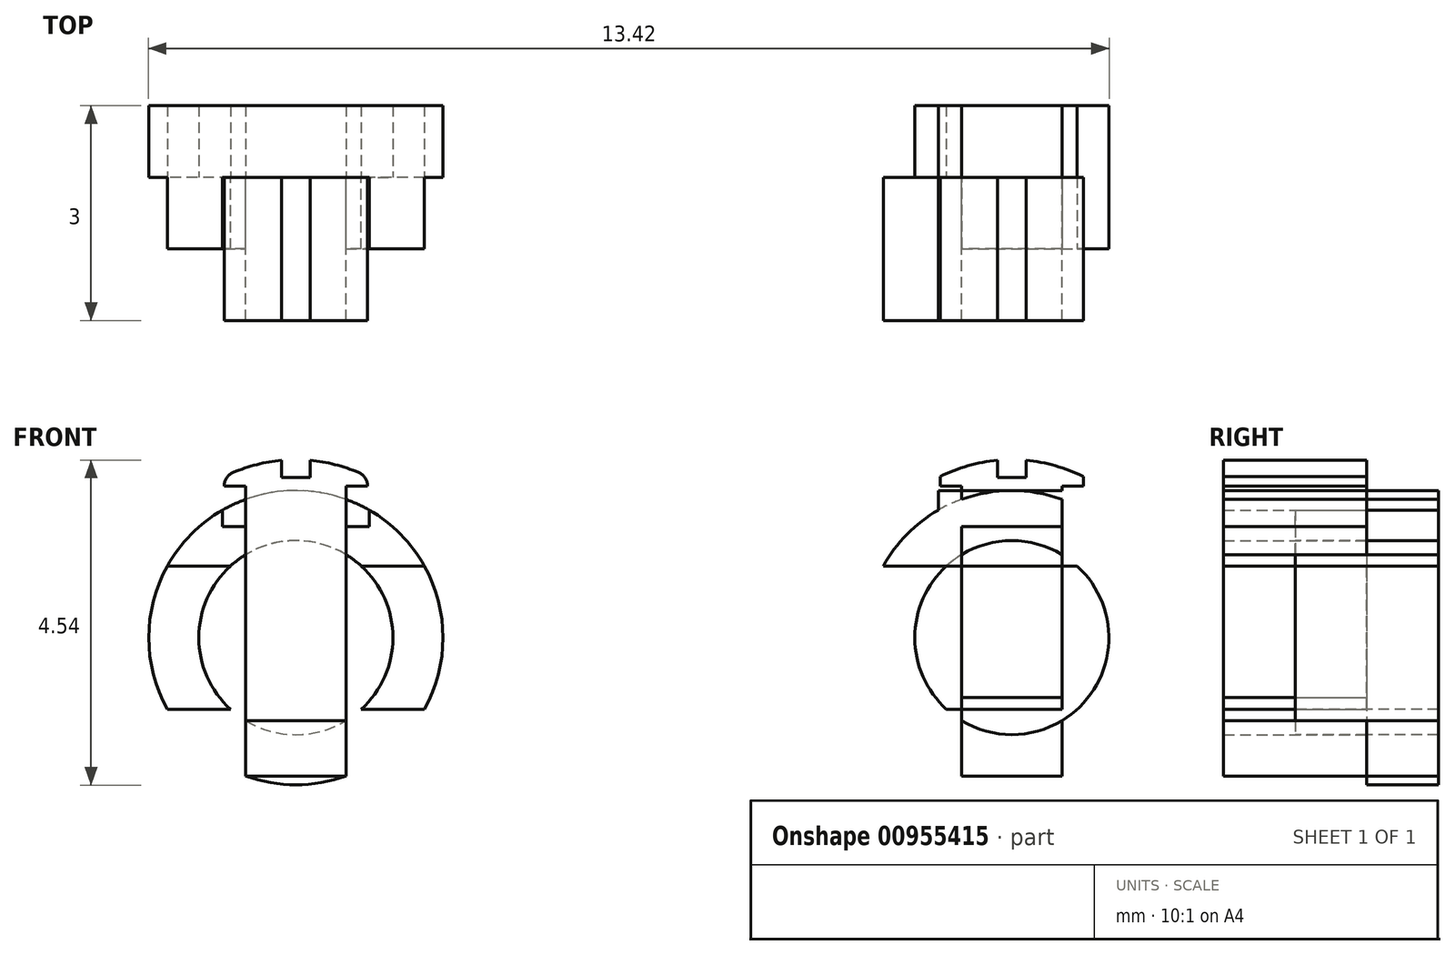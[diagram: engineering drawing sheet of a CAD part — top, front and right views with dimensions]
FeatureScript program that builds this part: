
annotation { "Feature Type Name" : "Feature", "Feature Type Description" : "" }
export const myFeature = defineFeature(function(context is Context, id is Id, definition is map)
    precondition{}
    {
        {
            var Q0;
            Q0=qCreatedBy(makeId("Front.planeOp"),FACE);
            var sketch = newSketch(context, id + "F0", { "sketchPlane" : qUnion([Q0])});
            skCircle(sketch, "E0", {"center": v(0, 0) * mm, "radius": 2.06 * mm});
            skLineSegment(sketch, "E1.bottom", {"start": v(2.5, 1) * mm, "end": v(-2.5, 1) * mm});
            skLineSegment(sketch, "E1.top", {"start": v(2.5, -1) * mm, "end": v(-2.5, -1) * mm});
            skLineSegment(sketch, "E1.left", {"start": v(2.5, 1) * mm, "end": v(2.5, -1) * mm});
            skLineSegment(sketch, "E1.right", {"start": v(-2.5, 1) * mm, "end": v(-2.5, -1) * mm});
            skCircle(sketch, "E2", {"center": v(0, 0) * mm, "radius": 1.35 * mm});
            skPoint(sketch, "E3", {"position": v(0, -1.35) * mm});
            skPoint(sketch, "E4", {"position": v(0, -2.06) * mm});
            skLineSegment(sketch, "E5.bottom", {"start": v(-0.7, 2.48) * mm, "end": v(0.7, 2.48) * mm});
            skLineSegment(sketch, "E5.top", {"start": v(-0.7, -1.93) * mm, "end": v(0.7, -1.93) * mm});
            skLineSegment(sketch, "E5.left", {"start": v(-0.7, 2.48) * mm, "end": v(-0.7, -1.93) * mm});
            skLineSegment(sketch, "E5.right", {"start": v(0.7, 2.48) * mm, "end": v(0.7, -1.93) * mm});
            skLineSegment(sketch, "E6.bottom", {"start": v(-1, 2.48) * mm, "end": v(1, 2.48) * mm});
            skLineSegment(sketch, "E6.top", {"start": v(-1, 2.11) * mm, "end": v(1, 2.11) * mm});
            skLineSegment(sketch, "E6.left", {"start": v(-1, 2.48) * mm, "end": v(-1, 2.11) * mm});
            skLineSegment(sketch, "E6.right", {"start": v(1, 2.48) * mm, "end": v(1, 2.11) * mm});
            skLineSegment(sketch, "E7", {"start": v(-0.7, -1.35) * mm, "end": v(0.7, -1.35) * mm});
            skPoint(sketch, "E8", {"position": v(-0.7, -1.16) * mm});
            skPoint(sketch, "E9", {"position": v(0.7, -1.16) * mm});
            skLineSegment(sketch, "E10", {"start": v(-0.7, -1.16) * mm, "end": v(0.7, -1.16) * mm});
            skLineSegment(sketch, "E11", {"start": v(5, 2.95) * mm, "end": v(5, -2.35) * mm});
            skLineSegment(sketch, "E12.MirrorCS", {"start": v(7.5, 1) * mm, "end": v(7.5, -1) * mm});
            skCircle(sketch, "E13.MirrorC", {"center": v(10, 0) * mm, "radius": 1.35 * mm});
            skLineSegment(sketch, "E14.MirrorCS", {"start": v(7.5, 1) * mm, "end": v(12.5, 1) * mm});
            skLineSegment(sketch, "E15.MirrorCS", {"start": v(7.5, -1) * mm, "end": v(12.5, -1) * mm});
            skLineSegment(sketch, "E16.MirrorCS", {"start": v(12.5, 1) * mm, "end": v(12.5, -1) * mm});
            skCircle(sketch, "E17.MirrorC", {"center": v(10, 0) * mm, "radius": 2.06 * mm});
            skLineSegment(sketch, "E18.MirrorCS", {"start": v(11, 2.49) * mm, "end": v(9, 2.49) * mm});
            skLineSegment(sketch, "E19.MirrorCS", {"start": v(11, 2.12) * mm, "end": v(9, 2.12) * mm});
            skLineSegment(sketch, "E20.MirrorCS", {"start": v(10.7, 2.49) * mm, "end": v(10.7, -1.93) * mm});
            skLineSegment(sketch, "E21.MirrorCS", {"start": v(9.3, 2.49) * mm, "end": v(9.3, -1.93) * mm});
            skLineSegment(sketch, "E22.MirrorCS", {"start": v(9, 2.49) * mm, "end": v(9, 2.12) * mm});
            skLineSegment(sketch, "E23.MirrorCS", {"start": v(11, 2.49) * mm, "end": v(11, 2.12) * mm});
            skLineSegment(sketch, "E24.MirrorCS", {"start": v(10.7, -1.93) * mm, "end": v(9.3, -1.93) * mm});
            skPoint(sketch, "E25", {"position": v(10, -2.06) * mm});
            skPoint(sketch, "E25.positionSnap0", {"position": v(10, -1.93) * mm});
            skLineSegment(sketch, "E26", {"start": v(9.3, -0.84) * mm, "end": v(10.7, -0.84) * mm});
            skLineSegment(sketch, "E27", {"start": v(9.3, -1.94) * mm, "end": v(10.7, -1.94) * mm});
            skPoint(sketch, "E28", {"position": v(9.3, -1.16) * mm});
            skLineSegment(sketch, "E29", {"start": v(10.7, -1.93) * mm, "end": v(10.7, -1.94) * mm});
            skLineSegment(sketch, "E30", {"start": v(9.3, -1.93) * mm, "end": v(9.3, -1.94) * mm});
            skLineSegment(sketch, "E31.bottom", {"start": v(-1.03, 1.55) * mm, "end": v(1.02, 1.55) * mm});
            skLineSegment(sketch, "E31.top", {"start": v(-1.03, 2.06) * mm, "end": v(1.02, 2.06) * mm});
            skLineSegment(sketch, "E31.left", {"start": v(-1.03, 1.55) * mm, "end": v(-1.03, 2.06) * mm});
            skLineSegment(sketch, "E31.right", {"start": v(1.02, 1.55) * mm, "end": v(1.02, 2.06) * mm});
            skLineSegment(sketch, "E32.MirrorCS", {"start": v(11.03, 1.55) * mm, "end": v(8.97, 1.55) * mm});
            skLineSegment(sketch, "E33.MirrorCS", {"start": v(8.97, 1.55) * mm, "end": v(8.97, 2.06) * mm});
            skLineSegment(sketch, "E34.MirrorCS", {"start": v(11.03, 2.06) * mm, "end": v(8.97, 2.06) * mm});
            skLineSegment(sketch, "E35.MirrorCS", {"start": v(11.03, 1.55) * mm, "end": v(11.03, 2.06) * mm});
            skSolve(sketch);
        }
        {
            var Q0;
            {var subQ0=sQuery(id+"F0.wireOp",EDGE,"E5.left");var subQ1=sQuery(id+"F0.wireOp",EDGE,"E0");var subQ2=makeQuery(id+"F0.imprint","INTERSECT",VERTEX,{"derivedFrom":[subQ1,subQ0]});Q0=makeQuery(id+"F0.imprint","IMPRINT",FACE,{"disambiguationData":[TD([[makeQuery(id+"F0.imprint","IMPRINT",EDGE,{"disambiguationData":[TD([[subQ2,-1.0]])],"derivedFrom":subQ1}),1.0]])]});}
            var Q1;
            {var subQ0=sQuery(id+"F0.wireOp",EDGE,"E5.right");var subQ1=sQuery(id+"F0.wireOp",EDGE,"E0");var subQ2=makeQuery(id+"F0.imprint","INTERSECT",VERTEX,{"derivedFrom":[subQ1,subQ0]});Q1=makeQuery(id+"F0.imprint","IMPRINT",FACE,{"disambiguationData":[TD([[makeQuery(id+"F0.imprint","IMPRINT",EDGE,{"disambiguationData":[TD([[subQ2,1.0]])],"derivedFrom":subQ1}),1.0]])]});}
            var Q2;
            {var subQ0=sQuery(id+"F0.wireOp",EDGE,"E1.bottom");var subQ1=sQuery(id+"F0.wireOp",EDGE,"E0");var subQ2=makeQuery(id+"F0.imprint","INTERSECT",VERTEX,{"disambiguationData":[OD(0.0)],"derivedFrom":[subQ1,subQ0]});Q2=makeQuery(id+"F0.imprint","IMPRINT",FACE,{"disambiguationData":[TD([[makeQuery(id+"F0.imprint","IMPRINT",EDGE,{"disambiguationData":[TD([[subQ2,1.0]])],"derivedFrom":subQ1}),1.0]])]});}
            var Q3;
            {var subQ0=sQuery(id+"F0.wireOp",EDGE,"E1.bottom");var subQ1=sQuery(id+"F0.wireOp",EDGE,"E0");var subQ2=makeQuery(id+"F0.imprint","INTERSECT",VERTEX,{"disambiguationData":[OD(1.0)],"derivedFrom":[subQ1,subQ0]});Q3=makeQuery(id+"F0.imprint","IMPRINT",FACE,{"disambiguationData":[TD([[makeQuery(id+"F0.imprint","IMPRINT",EDGE,{"disambiguationData":[TD([[subQ2,-1.0]])],"derivedFrom":subQ1}),1.0]])]});}
            var Q4;
            {var subQ3=sQuery(id+"F0.wireOp",EDGE,"E1.top");var subQ6=sQuery(id+"F0.wireOp",EDGE,"E0");var subQ7=makeQuery(id+"F0.imprint","INTERSECT",VERTEX,{"disambiguationData":[OD(0.0)],"derivedFrom":[subQ6,subQ3]});Q4=makeQuery(id+"F0.imprint","IMPRINT",FACE,{"disambiguationData":[TD([[makeQuery(id+"F0.imprint","IMPRINT",EDGE,{"disambiguationData":[TD([[subQ7,1.0]])],"derivedFrom":subQ3}),1.0]])]});}
            var Q5;
            {var subQ4=sQuery(id+"F0.wireOp",EDGE,"E1.top");var subQ6=sQuery(id+"F0.wireOp",EDGE,"E0");var subQ7=makeQuery(id+"F0.imprint","INTERSECT",VERTEX,{"disambiguationData":[OD(1.0)],"derivedFrom":[subQ6,subQ4]});Q5=makeQuery(id+"F0.imprint","IMPRINT",FACE,{"disambiguationData":[TD([[makeQuery(id+"F0.imprint","IMPRINT",EDGE,{"disambiguationData":[TD([[subQ7,-1.0]])],"derivedFrom":subQ4}),1.0]])]});}
            var Q6;
            {var subQ0=sQuery(id+"F0.wireOp",EDGE,"E5.top");Q6=makeQuery(id+"F0.imprint","IMPRINT",FACE,{"disambiguationData":[TD([[makeQuery(id+"F0.imprint","IMPRINT",EDGE,{"derivedFrom":subQ0}),-1.0]])]});}
            var Q7;
            {var subQ0=sQuery(id+"F0.wireOp",EDGE,"E5.right");var subQ3=sQuery(id+"F0.wireOp",EDGE,"E7");var subQ5=makeQuery(id+"F0.imprint","INTERSECT",VERTEX,{"derivedFrom":[subQ0,subQ3]});Q7=makeQuery(id+"F0.imprint","IMPRINT",FACE,{"disambiguationData":[TD([[makeQuery(id+"F0.imprint","IMPRINT",EDGE,{"disambiguationData":[TD([[subQ5,1.0]])],"derivedFrom":subQ3}),1.0]])]});}
            var Q8;
            {var subQ0=sQuery(id+"F0.wireOp",EDGE,"E5.left");var subQ3=sQuery(id+"F0.wireOp",EDGE,"E7");var subQ5=makeQuery(id+"F0.imprint","INTERSECT",VERTEX,{"derivedFrom":[subQ0,subQ3]});Q8=makeQuery(id+"F0.imprint","IMPRINT",FACE,{"disambiguationData":[TD([[makeQuery(id+"F0.imprint","IMPRINT",EDGE,{"disambiguationData":[TD([[subQ5,-1.0]])],"derivedFrom":subQ3}),1.0]])]});}
            var Q9;
            {var subQ1=sQuery(id+"F0.wireOp",EDGE,"E5.top");Q9=makeQuery(id+"F0.imprint","IMPRINT",FACE,{"disambiguationData":[TD([[makeQuery(id+"F0.imprint","IMPRINT",EDGE,{"derivedFrom":subQ1}),1.0]])]});}
            var Q10;
            {var subQ0=sQuery(id+"F0.wireOp",EDGE,"E5.right");var subQ1=sQuery(id+"F0.wireOp",EDGE,"E0");var subQ2=makeQuery(id+"F0.imprint","INTERSECT",VERTEX,{"derivedFrom":[subQ1,subQ0]});Q10=makeQuery(id+"F0.imprint","IMPRINT",FACE,{"disambiguationData":[TD([[makeQuery(id+"F0.imprint","IMPRINT",EDGE,{"disambiguationData":[TD([[subQ2,-1.0]])],"derivedFrom":subQ1}),1.0]])]});}
            var Q11;
            {var subQ0=sQuery(id+"F0.wireOp",EDGE,"E21.MirrorCS");var subQ1=sQuery(id+"F0.wireOp",EDGE,"E13.MirrorC");var subQ2=makeQuery(id+"F0.imprint","INTERSECT",VERTEX,{"disambiguationData":[OD(0.0)],"derivedFrom":[subQ1,subQ0]});Q11=makeQuery(id+"F0.imprint","IMPRINT",FACE,{"disambiguationData":[TD([[makeQuery(id+"F0.imprint","IMPRINT",EDGE,{"disambiguationData":[TD([[subQ2,1.0]])],"derivedFrom":subQ1}),1.0]])]});}
            var Q12;
            {var subQ0=sQuery(id+"F0.wireOp",EDGE,"3dWky65o-V6J0-wYT3-5itX-CX1B09bc3K4K");var subQ1=sQuery(id+"F0.wireOp",EDGE,"E17.MirrorC");var subQ2=makeQuery(id+"F0.imprint","INTERSECT",VERTEX,{"disambiguationData":[OD(0.0)],"derivedFrom":[subQ1,subQ0]});Q12=makeQuery(id+"F0.imprint","IMPRINT",FACE,{"disambiguationData":[TD([[makeQuery(id+"F0.imprint","IMPRINT",EDGE,{"disambiguationData":[TD([[subQ2,-1.0]])],"derivedFrom":subQ1}),-1.0]])]});}
            var Q13;
            {var subQ0=sQuery(id+"F0.wireOp",EDGE,"E21.MirrorCS");var subQ1=sQuery(id+"F0.wireOp",EDGE,"E13.MirrorC");var subQ2=makeQuery(id+"F0.imprint","INTERSECT",VERTEX,{"disambiguationData":[OD(0.0)],"derivedFrom":[subQ1,subQ0]});Q13=makeQuery(id+"F0.imprint","IMPRINT",FACE,{"disambiguationData":[TD([[makeQuery(id+"F0.imprint","IMPRINT",EDGE,{"disambiguationData":[TD([[subQ2,-1.0]])],"derivedFrom":subQ1}),1.0]])]});}
            var Q14;
            {var subQ0=sQuery(id+"F0.wireOp",EDGE,"E21.MirrorCS");var subQ1=sQuery(id+"F0.wireOp",EDGE,"E17.MirrorC");var subQ2=makeQuery(id+"F0.imprint","INTERSECT",VERTEX,{"derivedFrom":[subQ1,subQ0]});Q14=makeQuery(id+"F0.imprint","IMPRINT",FACE,{"disambiguationData":[TD([[makeQuery(id+"F0.imprint","IMPRINT",EDGE,{"disambiguationData":[TD([[subQ2,-1.0]])],"derivedFrom":subQ1}),-1.0]])]});}
            var Q15;
            {var subQ0=sQuery(id+"F0.wireOp",EDGE,"3dWky65o-V6J0-wYT3-5itX-CX1B09bc3K4K");var subQ1=sQuery(id+"F0.wireOp",EDGE,"E17.MirrorC");var subQ2=makeQuery(id+"F0.imprint","INTERSECT",VERTEX,{"disambiguationData":[OD(1.0)],"derivedFrom":[subQ1,subQ0]});Q15=makeQuery(id+"F0.imprint","IMPRINT",FACE,{"disambiguationData":[TD([[makeQuery(id+"F0.imprint","IMPRINT",EDGE,{"disambiguationData":[TD([[subQ2,1.0]])],"derivedFrom":subQ1}),-1.0]])]});}
            var Q16;
            {var subQ0=sQuery(id+"F0.wireOp",EDGE,"E20.MirrorCS");var subQ1=sQuery(id+"F0.wireOp",EDGE,"E13.MirrorC");var subQ2=makeQuery(id+"F0.imprint","INTERSECT",VERTEX,{"disambiguationData":[OD(0.0)],"derivedFrom":[subQ1,subQ0]});Q16=makeQuery(id+"F0.imprint","IMPRINT",FACE,{"disambiguationData":[TD([[makeQuery(id+"F0.imprint","IMPRINT",EDGE,{"disambiguationData":[TD([[subQ2,-1.0]])],"derivedFrom":subQ1}),1.0]])]});}
            var Q17;
            {var subQ0=sQuery(id+"F0.wireOp",EDGE,"E21.MirrorCS");var subQ1=sQuery(id+"F0.wireOp",EDGE,"E13.MirrorC");var subQ2=makeQuery(id+"F0.imprint","INTERSECT",VERTEX,{"disambiguationData":[OD(1.0)],"derivedFrom":[subQ1,subQ0]});Q17=makeQuery(id+"F0.imprint","IMPRINT",FACE,{"disambiguationData":[TD([[makeQuery(id+"F0.imprint","IMPRINT",EDGE,{"disambiguationData":[TD([[subQ2,-1.0]])],"derivedFrom":subQ1}),1.0]])]});}
            var Q18;
            {var subQ5=sQuery(id+"F0.wireOp",EDGE,"E24.MirrorCS");Q18=makeQuery(id+"F0.imprint","IMPRINT",FACE,{"disambiguationData":[TD([[makeQuery(id+"F0.imprint","IMPRINT",EDGE,{"derivedFrom":subQ5}),-1.0]])]});}
            var Q19;
            {var subQ0=sQuery(id+"F0.wireOp",EDGE,"E15.MirrorCS");var subQ1=sQuery(id+"F0.wireOp",EDGE,"E13.MirrorC");var subQ2=makeQuery(id+"F0.imprint","INTERSECT",VERTEX,{"disambiguationData":[OD(0.0)],"derivedFrom":[subQ1,subQ0]});Q19=makeQuery(id+"F0.imprint","IMPRINT",FACE,{"disambiguationData":[TD([[makeQuery(id+"F0.imprint","IMPRINT",EDGE,{"disambiguationData":[TD([[subQ2,-1.0]])],"derivedFrom":subQ1}),1.0]])]});}
            var Q20;
            {var subQ0=sQuery(id+"F0.wireOp",EDGE,"E14.MirrorCS");var subQ1=sQuery(id+"F0.wireOp",EDGE,"E13.MirrorC");var subQ2=makeQuery(id+"F0.imprint","INTERSECT",VERTEX,{"disambiguationData":[OD(0.0)],"derivedFrom":[subQ1,subQ0]});Q20=makeQuery(id+"F0.imprint","IMPRINT",FACE,{"disambiguationData":[TD([[makeQuery(id+"F0.imprint","IMPRINT",EDGE,{"disambiguationData":[TD([[subQ2,1.0]])],"derivedFrom":subQ1}),1.0]])]});}
            var Q21;
            {var subQ0=sQuery(id+"F0.wireOp",EDGE,"E27");var subQ1=sQuery(id+"F0.wireOp",EDGE,"E17.MirrorC");var subQ2=makeQuery(id+"F0.imprint","INTERSECT",VERTEX,{"disambiguationData":[OD(0.0)],"derivedFrom":[subQ1,subQ0]});Q21=makeQuery(id+"F0.imprint","IMPRINT",FACE,{"disambiguationData":[TD([[makeQuery(id+"F0.imprint","IMPRINT",EDGE,{"disambiguationData":[TD([[subQ2,-1.0]])],"derivedFrom":subQ1}),-1.0]])]});}
            var Q22;
            {var subQ0=sQuery(id+"F0.wireOp",EDGE,"E14.MirrorCS");var subQ1=sQuery(id+"F0.wireOp",EDGE,"E13.MirrorC");var subQ2=makeQuery(id+"F0.imprint","INTERSECT",VERTEX,{"disambiguationData":[OD(1.0)],"derivedFrom":[subQ1,subQ0]});Q22=makeQuery(id+"F0.imprint","IMPRINT",FACE,{"disambiguationData":[TD([[makeQuery(id+"F0.imprint","IMPRINT",EDGE,{"disambiguationData":[TD([[subQ2,-1.0]])],"derivedFrom":subQ1}),1.0]])]});}
            var Q23;
            {var subQ0=sQuery(id+"F0.wireOp",EDGE,"E24.MirrorCS");Q23=makeQuery(id+"F0.imprint","IMPRINT",FACE,{"disambiguationData":[TD([[makeQuery(id+"F0.imprint","IMPRINT",EDGE,{"derivedFrom":subQ0}),1.0]])]});}
            var Q24;
            {var subQ7=sQuery(id+"F0.wireOp",EDGE,"E0");var subQ9=sQuery(id+"F0.wireOp",EDGE,"E31.right");var subQ10=makeQuery(id+"F0.imprint","INTERSECT",VERTEX,{"derivedFrom":[subQ7,subQ9]});Q24=makeQuery(id+"F0.imprint","IMPRINT",FACE,{"disambiguationData":[TD([[makeQuery(id+"F0.imprint","IMPRINT",EDGE,{"disambiguationData":[TD([[subQ10,1.0]])],"derivedFrom":subQ7}),1.0]])]});}
            var Q25;
            {var subQ7=sQuery(id+"F0.wireOp",EDGE,"E31.left");var subQ9=sQuery(id+"F0.wireOp",EDGE,"E0");var subQ11=makeQuery(id+"F0.imprint","INTERSECT",VERTEX,{"derivedFrom":[subQ9,subQ7]});Q25=makeQuery(id+"F0.imprint","IMPRINT",FACE,{"disambiguationData":[TD([[makeQuery(id+"F0.imprint","IMPRINT",EDGE,{"disambiguationData":[TD([[subQ11,-1.0]])],"derivedFrom":subQ9}),1.0]])]});}
            var Q26;
            {var subQ0=sQuery(id+"F0.wireOp",EDGE,"E5.right");var subQ1=sQuery(id+"F0.wireOp",EDGE,"E2");var subQ2=makeQuery(id+"F0.imprint","INTERSECT",VERTEX,{"derivedFrom":[subQ1,subQ0]});Q26=makeQuery(id+"F0.imprint","IMPRINT",FACE,{"disambiguationData":[TD([[makeQuery(id+"F0.imprint","IMPRINT",EDGE,{"disambiguationData":[TD([[subQ2,-1.0]])],"derivedFrom":subQ1}),-1.0]])]});}
            var Q27;
            {var subQ0=sQuery(id+"F0.wireOp",EDGE,"E33.MirrorCS");var subQ1=sQuery(id+"F0.wireOp",EDGE,"E17.MirrorC");var subQ2=makeQuery(id+"F0.imprint","INTERSECT",VERTEX,{"derivedFrom":[subQ1,subQ0]});Q27=makeQuery(id+"F0.imprint","IMPRINT",FACE,{"disambiguationData":[TD([[makeQuery(id+"F0.imprint","IMPRINT",EDGE,{"disambiguationData":[TD([[subQ2,-1.0]])],"derivedFrom":subQ1}),-1.0]])]});}
            var Q28;
            {var subQ0=sQuery(id+"F0.wireOp",EDGE,"E35.MirrorCS");var subQ1=sQuery(id+"F0.wireOp",EDGE,"E17.MirrorC");var subQ2=makeQuery(id+"F0.imprint","INTERSECT",VERTEX,{"derivedFrom":[subQ1,subQ0]});Q28=makeQuery(id+"F0.imprint","IMPRINT",FACE,{"disambiguationData":[TD([[makeQuery(id+"F0.imprint","IMPRINT",EDGE,{"disambiguationData":[TD([[subQ2,1.0]])],"derivedFrom":subQ1}),-1.0]])]});}
            extrude(context, id + "F1", {"entities" : qUnion([Q0, Q1, Q2, Q3, Q4, Q5, Q6, Q7, Q8, Q9, Q10, Q11, Q12, Q13, Q14, Q15, Q16, Q17, Q18, Q19, Q20, Q21, Q22, Q23, Q24, Q25, Q26, Q27, Q28]), "oppositeDirection" : true, "depth" : 1 * mm, "offsetDistance" : 25 * mm});
        }
        {
            var Q0;
            {var subQ3=sQuery(id+"F0.wireOp",EDGE,"E1.top");var subQ6=sQuery(id+"F0.wireOp",EDGE,"E0");var subQ7=makeQuery(id+"F0.imprint","INTERSECT",VERTEX,{"disambiguationData":[OD(0.0)],"derivedFrom":[subQ6,subQ3]});Q0=makeQuery(id+"F0.imprint","IMPRINT",FACE,{"disambiguationData":[TD([[makeQuery(id+"F0.imprint","IMPRINT",EDGE,{"disambiguationData":[TD([[subQ7,1.0]])],"derivedFrom":subQ3}),1.0]])]});}
            var Q1;
            {var subQ4=sQuery(id+"F0.wireOp",EDGE,"E1.top");var subQ6=sQuery(id+"F0.wireOp",EDGE,"E0");var subQ7=makeQuery(id+"F0.imprint","INTERSECT",VERTEX,{"disambiguationData":[OD(1.0)],"derivedFrom":[subQ6,subQ4]});Q1=makeQuery(id+"F0.imprint","IMPRINT",FACE,{"disambiguationData":[TD([[makeQuery(id+"F0.imprint","IMPRINT",EDGE,{"disambiguationData":[TD([[subQ7,-1.0]])],"derivedFrom":subQ4}),1.0]])]});}
            var Q2;
            {var subQ0=sQuery(id+"F0.wireOp",EDGE,"E21.MirrorCS");var subQ1=sQuery(id+"F0.wireOp",EDGE,"E13.MirrorC");var subQ2=makeQuery(id+"F0.imprint","INTERSECT",VERTEX,{"disambiguationData":[OD(0.0)],"derivedFrom":[subQ1,subQ0]});Q2=makeQuery(id+"F0.imprint","IMPRINT",FACE,{"disambiguationData":[TD([[makeQuery(id+"F0.imprint","IMPRINT",EDGE,{"disambiguationData":[TD([[subQ2,1.0]])],"derivedFrom":subQ1}),1.0]])]});}
            var Q3;
            {var subQ0=sQuery(id+"F0.wireOp",EDGE,"3dWky65o-V6J0-wYT3-5itX-CX1B09bc3K4K");var subQ1=sQuery(id+"F0.wireOp",EDGE,"E17.MirrorC");var subQ2=makeQuery(id+"F0.imprint","INTERSECT",VERTEX,{"disambiguationData":[OD(0.0)],"derivedFrom":[subQ1,subQ0]});Q3=makeQuery(id+"F0.imprint","IMPRINT",FACE,{"disambiguationData":[TD([[makeQuery(id+"F0.imprint","IMPRINT",EDGE,{"disambiguationData":[TD([[subQ2,-1.0]])],"derivedFrom":subQ1}),-1.0]])]});}
            var Q4;
            {var subQ0=sQuery(id+"F0.wireOp",EDGE,"3dWky65o-V6J0-wYT3-5itX-CX1B09bc3K4K");var subQ1=sQuery(id+"F0.wireOp",EDGE,"E17.MirrorC");var subQ2=makeQuery(id+"F0.imprint","INTERSECT",VERTEX,{"disambiguationData":[OD(1.0)],"derivedFrom":[subQ1,subQ0]});Q4=makeQuery(id+"F0.imprint","IMPRINT",FACE,{"disambiguationData":[TD([[makeQuery(id+"F0.imprint","IMPRINT",EDGE,{"disambiguationData":[TD([[subQ2,1.0]])],"derivedFrom":subQ1}),-1.0]])]});}
            var Q5;
            {var subQ0=sQuery(id+"F0.wireOp",EDGE,"E20.MirrorCS");var subQ1=sQuery(id+"F0.wireOp",EDGE,"E13.MirrorC");var subQ2=makeQuery(id+"F0.imprint","INTERSECT",VERTEX,{"disambiguationData":[OD(0.0)],"derivedFrom":[subQ1,subQ0]});Q5=makeQuery(id+"F0.imprint","IMPRINT",FACE,{"disambiguationData":[TD([[makeQuery(id+"F0.imprint","IMPRINT",EDGE,{"disambiguationData":[TD([[subQ2,-1.0]])],"derivedFrom":subQ1}),1.0]])]});}
            var Q6;
            {var subQ0=sQuery(id+"F0.wireOp",EDGE,"E15.MirrorCS");var subQ1=sQuery(id+"F0.wireOp",EDGE,"E13.MirrorC");var subQ2=makeQuery(id+"F0.imprint","INTERSECT",VERTEX,{"disambiguationData":[OD(0.0)],"derivedFrom":[subQ1,subQ0]});Q6=makeQuery(id+"F0.imprint","IMPRINT",FACE,{"disambiguationData":[TD([[makeQuery(id+"F0.imprint","IMPRINT",EDGE,{"disambiguationData":[TD([[subQ2,-1.0]])],"derivedFrom":subQ1}),1.0]])]});}
            var Q7;
            {var subQ0=sQuery(id+"F0.wireOp",EDGE,"E21.MirrorCS");var subQ1=sQuery(id+"F0.wireOp",EDGE,"E13.MirrorC");var subQ2=makeQuery(id+"F0.imprint","INTERSECT",VERTEX,{"disambiguationData":[OD(1.0)],"derivedFrom":[subQ1,subQ0]});Q7=makeQuery(id+"F0.imprint","IMPRINT",FACE,{"disambiguationData":[TD([[makeQuery(id+"F0.imprint","IMPRINT",EDGE,{"disambiguationData":[TD([[subQ2,-1.0]])],"derivedFrom":subQ1}),1.0]])]});}
            var Q8;
            {var subQ7=sQuery(id+"F0.wireOp",EDGE,"E31.left");var subQ9=sQuery(id+"F0.wireOp",EDGE,"E0");var subQ11=makeQuery(id+"F0.imprint","INTERSECT",VERTEX,{"derivedFrom":[subQ9,subQ7]});Q8=makeQuery(id+"F0.imprint","IMPRINT",FACE,{"disambiguationData":[TD([[makeQuery(id+"F0.imprint","IMPRINT",EDGE,{"disambiguationData":[TD([[subQ11,-1.0]])],"derivedFrom":subQ9}),1.0]])]});}
            var Q9;
            {var subQ7=sQuery(id+"F0.wireOp",EDGE,"E0");var subQ9=sQuery(id+"F0.wireOp",EDGE,"E31.right");var subQ10=makeQuery(id+"F0.imprint","INTERSECT",VERTEX,{"derivedFrom":[subQ7,subQ9]});Q9=makeQuery(id+"F0.imprint","IMPRINT",FACE,{"disambiguationData":[TD([[makeQuery(id+"F0.imprint","IMPRINT",EDGE,{"disambiguationData":[TD([[subQ10,1.0]])],"derivedFrom":subQ7}),1.0]])]});}
            extrude(context, id + "F2", {"entities" : qUnion([Q0, Q1, Q2, Q3, Q4, Q5, Q6, Q7, Q8, Q9]), "operationType" : NewBodyOperationType.ADD, "depth" : 1 * mm, "offsetDistance" : 25 * mm});
        }
        {
            var Q0;
            {var subQ0=sQuery(id+"F0.wireOp",EDGE,"E6.bottom");var subQ1=sQuery(id+"F0.wireOp",EDGE,"E5.left");var subQ2=makeQuery(id+"F0.imprint","INTERSECT",VERTEX,{"derivedFrom":[subQ1,subQ0]});Q0=makeQuery(id+"F0.imprint","IMPRINT",FACE,{"disambiguationData":[TD([[makeQuery(id+"F0.imprint","IMPRINT",EDGE,{"disambiguationData":[TD([[subQ2,-1.0]])],"derivedFrom":subQ1}),1.0]])]});}
            var Q1;
            {var subQ5=sQuery(id+"F0.wireOp",EDGE,"E6.left");Q1=makeQuery(id+"F0.imprint","IMPRINT",FACE,{"disambiguationData":[TD([[makeQuery(id+"F0.imprint","IMPRINT",EDGE,{"derivedFrom":subQ5}),1.0]])]});}
            var Q2;
            {var subQ5=sQuery(id+"F0.wireOp",EDGE,"E6.right");Q2=makeQuery(id+"F0.imprint","IMPRINT",FACE,{"disambiguationData":[TD([[makeQuery(id+"F0.imprint","IMPRINT",EDGE,{"derivedFrom":subQ5}),-1.0]])]});}
            var Q3;
            {var subQ0=sQuery(id+"F0.wireOp",EDGE,"E5.right");var subQ1=sQuery(id+"F0.wireOp",EDGE,"E0");var subQ2=makeQuery(id+"F0.imprint","INTERSECT",VERTEX,{"derivedFrom":[subQ1,subQ0]});Q3=makeQuery(id+"F0.imprint","IMPRINT",FACE,{"disambiguationData":[TD([[makeQuery(id+"F0.imprint","IMPRINT",EDGE,{"disambiguationData":[TD([[subQ2,-1.0]])],"derivedFrom":subQ1}),1.0]])]});}
            var Q4;
            {var subQ0=sQuery(id+"F0.wireOp",EDGE,"E5.right");var subQ1=sQuery(id+"F0.wireOp",EDGE,"E0");var subQ2=makeQuery(id+"F0.imprint","INTERSECT",VERTEX,{"derivedFrom":[subQ1,subQ0]});Q4=makeQuery(id+"F0.imprint","IMPRINT",FACE,{"disambiguationData":[TD([[makeQuery(id+"F0.imprint","IMPRINT",EDGE,{"disambiguationData":[TD([[subQ2,-1.0]])],"derivedFrom":subQ1}),-1.0]])]});}
            var Q5;
            {var subQ1=sQuery(id+"F0.wireOp",EDGE,"E5.left");var subQ4=sQuery(id+"F0.wireOp",EDGE,"E6.top");var subQ5=makeQuery(id+"F0.imprint","INTERSECT",VERTEX,{"derivedFrom":[subQ1,subQ4]});Q5=makeQuery(id+"F0.imprint","IMPRINT",FACE,{"disambiguationData":[TD([[makeQuery(id+"F0.imprint","IMPRINT",EDGE,{"disambiguationData":[TD([[subQ5,-1.0]])],"derivedFrom":subQ1}),1.0]])]});}
            var Q6;
            {var subQ0=sQuery(id+"F0.wireOp",EDGE,"E31.top");var subQ1=sQuery(id+"F0.wireOp",EDGE,"E0");var subQ2=makeQuery(id+"F0.imprint","INTERSECT",VERTEX,{"derivedFrom":[subQ1,subQ0]});Q6=makeQuery(id+"F0.imprint","IMPRINT",FACE,{"disambiguationData":[TD([[makeQuery(id+"F0.imprint","IMPRINT",EDGE,{"disambiguationData":[TD([[subQ2,-1.0]])],"derivedFrom":subQ1}),-1.0]])]});}
            var Q7;
            {var subQ0=sQuery(id+"F0.wireOp",EDGE,"E5.right");var subQ1=sQuery(id+"F0.wireOp",EDGE,"E2");var subQ2=makeQuery(id+"F0.imprint","INTERSECT",VERTEX,{"derivedFrom":[subQ1,subQ0]});Q7=makeQuery(id+"F0.imprint","IMPRINT",FACE,{"disambiguationData":[TD([[makeQuery(id+"F0.imprint","IMPRINT",EDGE,{"disambiguationData":[TD([[subQ2,-1.0]])],"derivedFrom":subQ1}),-1.0]])]});}
            var Q8;
            {var subQ0=sQuery(id+"F0.wireOp",EDGE,"E5.right");var subQ1=sQuery(id+"F0.wireOp",EDGE,"E1.bottom");var subQ2=makeQuery(id+"F0.imprint","INTERSECT",VERTEX,{"derivedFrom":[subQ1,subQ0]});Q8=makeQuery(id+"F0.imprint","IMPRINT",FACE,{"disambiguationData":[TD([[makeQuery(id+"F0.imprint","IMPRINT",EDGE,{"disambiguationData":[TD([[subQ2,-1.0]])],"derivedFrom":subQ1}),-1.0]])]});}
            var Q9;
            {var subQ0=sQuery(id+"F0.wireOp",EDGE,"E5.right");var subQ1=sQuery(id+"F0.wireOp",EDGE,"E1.bottom");var subQ2=makeQuery(id+"F0.imprint","INTERSECT",VERTEX,{"derivedFrom":[subQ1,subQ0]});Q9=makeQuery(id+"F0.imprint","IMPRINT",FACE,{"disambiguationData":[TD([[makeQuery(id+"F0.imprint","IMPRINT",EDGE,{"disambiguationData":[TD([[subQ2,-1.0]])],"derivedFrom":subQ1}),1.0]])]});}
            var Q10;
            {var subQ5=sQuery(id+"F0.wireOp",EDGE,"E10");Q10=makeQuery(id+"F0.imprint","IMPRINT",FACE,{"disambiguationData":[TD([[makeQuery(id+"F0.imprint","IMPRINT",EDGE,{"derivedFrom":subQ5}),1.0]])]});}
            var Q11;
            {var subQ0=sQuery(id+"F0.wireOp",EDGE,"E22.MirrorCS");Q11=makeQuery(id+"F0.imprint","IMPRINT",FACE,{"disambiguationData":[TD([[makeQuery(id+"F0.imprint","IMPRINT",EDGE,{"derivedFrom":subQ0}),1.0]])]});}
            var Q12;
            {var subQ0=sQuery(id+"F0.wireOp",EDGE,"E20.MirrorCS");var subQ1=sQuery(id+"F0.wireOp",EDGE,"E18.MirrorCS");var subQ2=makeQuery(id+"F0.imprint","INTERSECT",VERTEX,{"derivedFrom":[subQ1,subQ0]});Q12=makeQuery(id+"F0.imprint","IMPRINT",FACE,{"disambiguationData":[TD([[makeQuery(id+"F0.imprint","IMPRINT",EDGE,{"disambiguationData":[TD([[subQ2,-1.0]])],"derivedFrom":subQ1}),1.0]])]});}
            var Q13;
            {var subQ0=sQuery(id+"F0.wireOp",EDGE,"E23.MirrorCS");Q13=makeQuery(id+"F0.imprint","IMPRINT",FACE,{"disambiguationData":[TD([[makeQuery(id+"F0.imprint","IMPRINT",EDGE,{"derivedFrom":subQ0}),-1.0]])]});}
            var Q14;
            {var subQ0=sQuery(id+"F0.wireOp",EDGE,"E21.MirrorCS");var subQ1=sQuery(id+"F0.wireOp",EDGE,"E17.MirrorC");var subQ2=makeQuery(id+"F0.imprint","INTERSECT",VERTEX,{"derivedFrom":[subQ1,subQ0]});Q14=makeQuery(id+"F0.imprint","IMPRINT",FACE,{"disambiguationData":[TD([[makeQuery(id+"F0.imprint","IMPRINT",EDGE,{"disambiguationData":[TD([[subQ2,-1.0]])],"derivedFrom":subQ1}),-1.0]])]});}
            var Q15;
            {var subQ0=sQuery(id+"F0.wireOp",EDGE,"E21.MirrorCS");var subQ1=sQuery(id+"F0.wireOp",EDGE,"E17.MirrorC");var subQ2=makeQuery(id+"F0.imprint","INTERSECT",VERTEX,{"derivedFrom":[subQ1,subQ0]});Q15=makeQuery(id+"F0.imprint","IMPRINT",FACE,{"disambiguationData":[TD([[makeQuery(id+"F0.imprint","IMPRINT",EDGE,{"disambiguationData":[TD([[subQ2,-1.0]])],"derivedFrom":subQ1}),1.0]])]});}
            var Q16;
            {var subQ1=sQuery(id+"F0.wireOp",EDGE,"E20.MirrorCS");var subQ5=sQuery(id+"F0.wireOp",EDGE,"E19.MirrorCS");var subQ8=makeQuery(id+"F0.imprint","INTERSECT",VERTEX,{"derivedFrom":[subQ5,subQ1]});Q16=makeQuery(id+"F0.imprint","IMPRINT",FACE,{"disambiguationData":[TD([[makeQuery(id+"F0.imprint","IMPRINT",EDGE,{"disambiguationData":[TD([[subQ8,-1.0]])],"derivedFrom":subQ5}),1.0]])]});}
            var Q17;
            {var subQ0=sQuery(id+"F0.wireOp",EDGE,"E34.MirrorCS");var subQ1=sQuery(id+"F0.wireOp",EDGE,"E17.MirrorC");var subQ2=makeQuery(id+"F0.imprint","INTERSECT",VERTEX,{"derivedFrom":[subQ1,subQ0]});Q17=makeQuery(id+"F0.imprint","IMPRINT",FACE,{"disambiguationData":[TD([[makeQuery(id+"F0.imprint","IMPRINT",EDGE,{"disambiguationData":[TD([[subQ2,-1.0]])],"derivedFrom":subQ1}),1.0]])]});}
            var Q18;
            {var subQ0=sQuery(id+"F0.wireOp",EDGE,"E21.MirrorCS");var subQ1=sQuery(id+"F0.wireOp",EDGE,"E13.MirrorC");var subQ2=makeQuery(id+"F0.imprint","INTERSECT",VERTEX,{"disambiguationData":[OD(0.0)],"derivedFrom":[subQ1,subQ0]});Q18=makeQuery(id+"F0.imprint","IMPRINT",FACE,{"disambiguationData":[TD([[makeQuery(id+"F0.imprint","IMPRINT",EDGE,{"disambiguationData":[TD([[subQ2,-1.0]])],"derivedFrom":subQ1}),1.0]])]});}
            var Q19;
            {var subQ0=sQuery(id+"F0.wireOp",EDGE,"E21.MirrorCS");var subQ1=sQuery(id+"F0.wireOp",EDGE,"E13.MirrorC");var subQ2=makeQuery(id+"F0.imprint","INTERSECT",VERTEX,{"disambiguationData":[OD(0.0)],"derivedFrom":[subQ1,subQ0]});Q19=makeQuery(id+"F0.imprint","IMPRINT",FACE,{"disambiguationData":[TD([[makeQuery(id+"F0.imprint","IMPRINT",EDGE,{"disambiguationData":[TD([[subQ2,-1.0]])],"derivedFrom":subQ1}),-1.0]])]});}
            var Q20;
            {var subQ5=sQuery(id+"F0.wireOp",EDGE,"E26");Q20=makeQuery(id+"F0.imprint","IMPRINT",FACE,{"disambiguationData":[TD([[makeQuery(id+"F0.imprint","IMPRINT",EDGE,{"derivedFrom":subQ5}),1.0]])]});}
            extrude(context, id + "F3", {"entities" : qUnion([Q0, Q1, Q2, Q3, Q4, Q5, Q6, Q7, Q8, Q9, Q10, Q11, Q12, Q13, Q14, Q15, Q16, Q17, Q18, Q19, Q20]), "depth" : 2 * mm, "offsetDistance" : 25 * mm});
        }
        {
            var Q0;
            {var subQ5=sQuery(id+"F0.wireOp",EDGE,"E26");Q0=makeQuery(id+"F0.imprint","IMPRINT",FACE,{"disambiguationData":[TD([[makeQuery(id+"F0.imprint","IMPRINT",EDGE,{"derivedFrom":subQ5}),-1.0]])]});}
            var Q1;
            {var subQ0=sQuery(id+"F0.wireOp",EDGE,"E20.MirrorCS");var subQ1=sQuery(id+"F0.wireOp",EDGE,"E13.MirrorC");var subQ2=makeQuery(id+"F0.imprint","INTERSECT",VERTEX,{"disambiguationData":[OD(1.0)],"derivedFrom":[subQ1,subQ0]});Q1=makeQuery(id+"F0.imprint","IMPRINT",FACE,{"disambiguationData":[TD([[makeQuery(id+"F0.imprint","IMPRINT",EDGE,{"disambiguationData":[TD([[subQ2,-1.0]])],"derivedFrom":subQ1}),-1.0]])]});}
            var Q2;
            {var subQ5=sQuery(id+"F0.wireOp",EDGE,"E24.MirrorCS");Q2=makeQuery(id+"F0.imprint","IMPRINT",FACE,{"disambiguationData":[TD([[makeQuery(id+"F0.imprint","IMPRINT",EDGE,{"derivedFrom":subQ5}),-1.0]])]});}
            var Q3;
            {var subQ0=sQuery(id+"F0.wireOp",EDGE,"E30");Q3=makeQuery(id+"F0.imprint","IMPRINT",FACE,{"disambiguationData":[TD([[makeQuery(id+"F0.imprint","IMPRINT",EDGE,{"derivedFrom":subQ0}),1.0]])]});}
            var Q4;
            {var subQ0=sQuery(id+"F0.wireOp",EDGE,"E24.MirrorCS");Q4=makeQuery(id+"F0.imprint","IMPRINT",FACE,{"disambiguationData":[TD([[makeQuery(id+"F0.imprint","IMPRINT",EDGE,{"derivedFrom":subQ0}),1.0]])]});}
            var Q5;
            {var subQ0=sQuery(id+"F0.wireOp",EDGE,"E29");Q5=makeQuery(id+"F0.imprint","IMPRINT",FACE,{"disambiguationData":[TD([[makeQuery(id+"F0.imprint","IMPRINT",EDGE,{"derivedFrom":subQ0}),-1.0]])]});}
            var Q6;
            {var subQ0=sQuery(id+"F0.wireOp",EDGE,"E10");Q6=makeQuery(id+"F0.imprint","IMPRINT",FACE,{"disambiguationData":[TD([[makeQuery(id+"F0.imprint","IMPRINT",EDGE,{"derivedFrom":subQ0}),-1.0]])]});}
            var Q7;
            {var subQ0=sQuery(id+"F0.wireOp",EDGE,"E5.left");var subQ3=sQuery(id+"F0.wireOp",EDGE,"E7");var subQ5=makeQuery(id+"F0.imprint","INTERSECT",VERTEX,{"derivedFrom":[subQ0,subQ3]});Q7=makeQuery(id+"F0.imprint","IMPRINT",FACE,{"disambiguationData":[TD([[makeQuery(id+"F0.imprint","IMPRINT",EDGE,{"disambiguationData":[TD([[subQ5,-1.0]])],"derivedFrom":subQ3}),1.0]])]});}
            var Q8;
            {var subQ0=sQuery(id+"F0.wireOp",EDGE,"E5.right");var subQ3=sQuery(id+"F0.wireOp",EDGE,"E7");var subQ5=makeQuery(id+"F0.imprint","INTERSECT",VERTEX,{"derivedFrom":[subQ0,subQ3]});Q8=makeQuery(id+"F0.imprint","IMPRINT",FACE,{"disambiguationData":[TD([[makeQuery(id+"F0.imprint","IMPRINT",EDGE,{"disambiguationData":[TD([[subQ5,1.0]])],"derivedFrom":subQ3}),1.0]])]});}
            var Q9;
            {var subQ5=sQuery(id+"F0.wireOp",EDGE,"E5.top");Q9=makeQuery(id+"F0.imprint","IMPRINT",FACE,{"disambiguationData":[TD([[makeQuery(id+"F0.imprint","IMPRINT",EDGE,{"derivedFrom":subQ5}),1.0]])]});}
            extrude(context, id + "F4", {"entities" : qUnion([Q0, Q1, Q2, Q3, Q4, Q5, Q6, Q7, Q8, Q9]), "depth" : 2 * mm, "offsetDistance" : 25 * mm});
        }
        {
            var Q0;
            Q0=makeQuery(id+"F3.opExtrude","CAP_FACE",FACE,{"disambiguationData":[OSD([sQuery(id+"F0.wireOp",EDGE,"E18.MirrorCS"),sQuery(id+"F0.wireOp",EDGE,"E19.MirrorCS"),sQuery(id+"F0.wireOp",EDGE,"E20.MirrorCS"),sQuery(id+"F0.wireOp",EDGE,"E21.MirrorCS"),sQuery(id+"F0.wireOp",EDGE,"E22.MirrorCS"),sQuery(id+"F0.wireOp",EDGE,"E23.MirrorCS"),sQuery(id+"F0.wireOp",EDGE,"E26")])],"isStart":false});
            var sketch = newSketch(context, id + "F5", { "sketchPlane" : qUnion([Q0])});
            skCircle(sketch, "E36", {"center": v(0, 0.23) * mm, "radius": 2.25 * mm});
            skCircle(sketch, "E37", {"center": v(10, 0.24) * mm, "radius": 2.25 * mm});
            skPoint(sketch, "E37.centerSnap0", {"position": v(10, -0.84) * mm});
            skLineSegment(sketch, "E38.bottom", {"start": v(1.26, 2.96) * mm, "end": v(-1.26, 2.96) * mm});
            skLineSegment(sketch, "E38.top", {"start": v(1.26, 2.01) * mm, "end": v(-1.26, 2.01) * mm});
            skLineSegment(sketch, "E38.left", {"start": v(1.26, 2.96) * mm, "end": v(1.26, 2.01) * mm});
            skLineSegment(sketch, "E38.right", {"start": v(-1.26, 2.96) * mm, "end": v(-1.26, 2.01) * mm});
            skPoint(sketch, "E38.middle", {"position": v(0, 2.48) * mm});
            skLineSegment(sketch, "E39.bottom", {"start": v(11.42, 2.95) * mm, "end": v(8.58, 2.95) * mm});
            skLineSegment(sketch, "E39.top", {"start": v(11.42, 2.02) * mm, "end": v(8.58, 2.02) * mm});
            skLineSegment(sketch, "E39.left", {"start": v(11.42, 2.95) * mm, "end": v(11.42, 2.02) * mm});
            skLineSegment(sketch, "E39.right", {"start": v(8.58, 2.95) * mm, "end": v(8.58, 2.02) * mm});
            skPoint(sketch, "E39.middle", {"position": v(10, 2.49) * mm});
            skLineSegment(sketch, "E40.bottom", {"start": v(0.2, 2.73) * mm, "end": v(-0.2, 2.73) * mm});
            skLineSegment(sketch, "E40.top", {"start": v(0.2, 2.23) * mm, "end": v(-0.2, 2.23) * mm});
            skLineSegment(sketch, "E40.left", {"start": v(0.2, 2.73) * mm, "end": v(0.2, 2.23) * mm});
            skLineSegment(sketch, "E40.right", {"start": v(-0.2, 2.73) * mm, "end": v(-0.2, 2.23) * mm});
            skLineSegment(sketch, "E41.bottom", {"start": v(10.2, 2.73) * mm, "end": v(9.8, 2.73) * mm});
            skLineSegment(sketch, "E41.top", {"start": v(10.2, 2.24) * mm, "end": v(9.8, 2.24) * mm});
            skLineSegment(sketch, "E41.left", {"start": v(10.2, 2.73) * mm, "end": v(10.2, 2.24) * mm});
            skLineSegment(sketch, "E41.right", {"start": v(9.8, 2.73) * mm, "end": v(9.8, 2.24) * mm});
            skSolve(sketch);
        }
        {
            var Q0;
            {var subQ1=sQuery(id+"F5.wireOp",EDGE,"E38.bottom");Q0=makeQuery(id+"F5.imprint","IMPRINT",FACE,{"disambiguationData":[TD([[makeQuery(id+"F5.imprint","IMPRINT",EDGE,{"derivedFrom":subQ1}),1.0]])]});}
            var Q1;
            {var subQ5=sQuery(id+"F5.wireOp",EDGE,"E40.top");Q1=makeQuery(id+"F5.imprint","IMPRINT",FACE,{"disambiguationData":[TD([[makeQuery(id+"F5.imprint","IMPRINT",EDGE,{"derivedFrom":subQ5}),-1.0]])]});}
            var Q2;
            {var subQ5=sQuery(id+"F5.wireOp",EDGE,"E40.bottom");Q2=makeQuery(id+"F5.imprint","IMPRINT",FACE,{"disambiguationData":[TD([[makeQuery(id+"F5.imprint","IMPRINT",EDGE,{"derivedFrom":subQ5}),1.0]])]});}
            var Q3;
            {var subQ0=sQuery(id+"F5.wireOp",EDGE,"E41.right");var subQ1=sQuery(id+"F5.wireOp",EDGE,"E37");var subQ2=makeQuery(id+"F5.imprint","INTERSECT",VERTEX,{"derivedFrom":[subQ1,subQ0]});Q3=makeQuery(id+"F5.imprint","IMPRINT",FACE,{"disambiguationData":[TD([[makeQuery(id+"F5.imprint","IMPRINT",EDGE,{"disambiguationData":[TD([[subQ2,-1.0]])],"derivedFrom":subQ1}),-1.0]])]});}
            var Q4;
            {var subQ0=sQuery(id+"F5.wireOp",EDGE,"E41.left");var subQ1=sQuery(id+"F5.wireOp",EDGE,"E37");var subQ2=makeQuery(id+"F5.imprint","INTERSECT",VERTEX,{"derivedFrom":[subQ1,subQ0]});Q4=makeQuery(id+"F5.imprint","IMPRINT",FACE,{"disambiguationData":[TD([[makeQuery(id+"F5.imprint","IMPRINT",EDGE,{"disambiguationData":[TD([[subQ2,1.0]])],"derivedFrom":subQ1}),-1.0]])]});}
            var Q5;
            {var subQ1=sQuery(id+"F5.wireOp",EDGE,"E41.top");Q5=makeQuery(id+"F5.imprint","IMPRINT",FACE,{"disambiguationData":[TD([[makeQuery(id+"F5.imprint","IMPRINT",EDGE,{"derivedFrom":subQ1}),-1.0]])]});}
            var Q6;
            {var subQ4=sQuery(id+"F5.wireOp",EDGE,"E41.bottom");Q6=makeQuery(id+"F5.imprint","IMPRINT",FACE,{"disambiguationData":[TD([[makeQuery(id+"F5.imprint","IMPRINT",EDGE,{"derivedFrom":subQ4}),1.0]])]});}
            extrude(context, id + "F6", {"entities" : qUnion([Q0, Q1, Q2, Q3, Q4, Q5, Q6]), "operationType" : NewBodyOperationType.REMOVE, "endBound" : BoundingType.THROUGH_ALL, "oppositeDirection" : true, "depth" : 25 * mm, "offsetDistance" : 25 * mm});
        }
        {
            var Q0;
            {var subQ0=sQuery(id+"F5.wireOp",EDGE,"E36");Q0=makeQuery(id+"F6.boolean.opBoolean","INTERSECT",EDGE,{"derivedFrom":[makeQuery(id+"F3.opExtrude","SWEPT_FACE",FACE,{"disambiguationData":[OSD([sQuery(id+"F0.wireOp",EDGE,"E6.left")])]}),makeQuery(id+"F6.opExtrude","SWEPT_FACE",FACE,{"disambiguationData":[OSD([subQ0]),TDD([makeQuery(id+"F5.imprint","IMPRINT",EDGE,{"disambiguationData":[TD([[makeQuery(id+"F5.imprint","INTERSECT",VERTEX,{"derivedFrom":[subQ0,sQuery(id+"F5.wireOp",EDGE,"E38.right")]}),1.0]])],"derivedFrom":subQ0})])]})]});}
            var Q1;
            {var subQ0=sQuery(id+"F5.wireOp",EDGE,"E36");Q1=makeQuery(id+"F6.boolean.opBoolean","INTERSECT",EDGE,{"derivedFrom":[makeQuery(id+"F3.opExtrude","SWEPT_FACE",FACE,{"disambiguationData":[OSD([sQuery(id+"F0.wireOp",EDGE,"E6.right")])]}),makeQuery(id+"F6.opExtrude","SWEPT_FACE",FACE,{"disambiguationData":[OSD([subQ0]),TDD([makeQuery(id+"F5.imprint","IMPRINT",EDGE,{"disambiguationData":[TD([[makeQuery(id+"F5.imprint","INTERSECT",VERTEX,{"derivedFrom":[subQ0,sQuery(id+"F5.wireOp",EDGE,"E38.left")]}),-1.0]])],"derivedFrom":subQ0})])]})]});}
            var Q2;
            Q2=makeQuery(id+"F6.boolean.opBoolean","COPY",EDGE,{"derivedFrom":makeQuery(id+"F6.opExtrude","SWEPT_EDGE",EDGE,{"disambiguationData":[OSD([sQuery(id+"F0.wireOp",EDGE,"E23.MirrorCS"),sQuery(id+"F5.wireOp",EDGE,"E37")])]})});
            var Q3;
            Q3=makeQuery(id+"F6.boolean.opBoolean","COPY",EDGE,{"derivedFrom":makeQuery(id+"F6.opExtrude","SWEPT_EDGE",EDGE,{"disambiguationData":[OSD([sQuery(id+"F0.wireOp",EDGE,"E22.MirrorCS"),sQuery(id+"F5.wireOp",EDGE,"E37")])]})});
            fillet(context, id + "F7", {"entities" : qUnion([Q0, Q1, Q2, Q3]), "tangentPropagation" : true, "radius" : 0.2 * mm, "defaultsChanged" : true, "vertexSettings" : [], "allowEdgeOverflow" : false});
        }
    });
